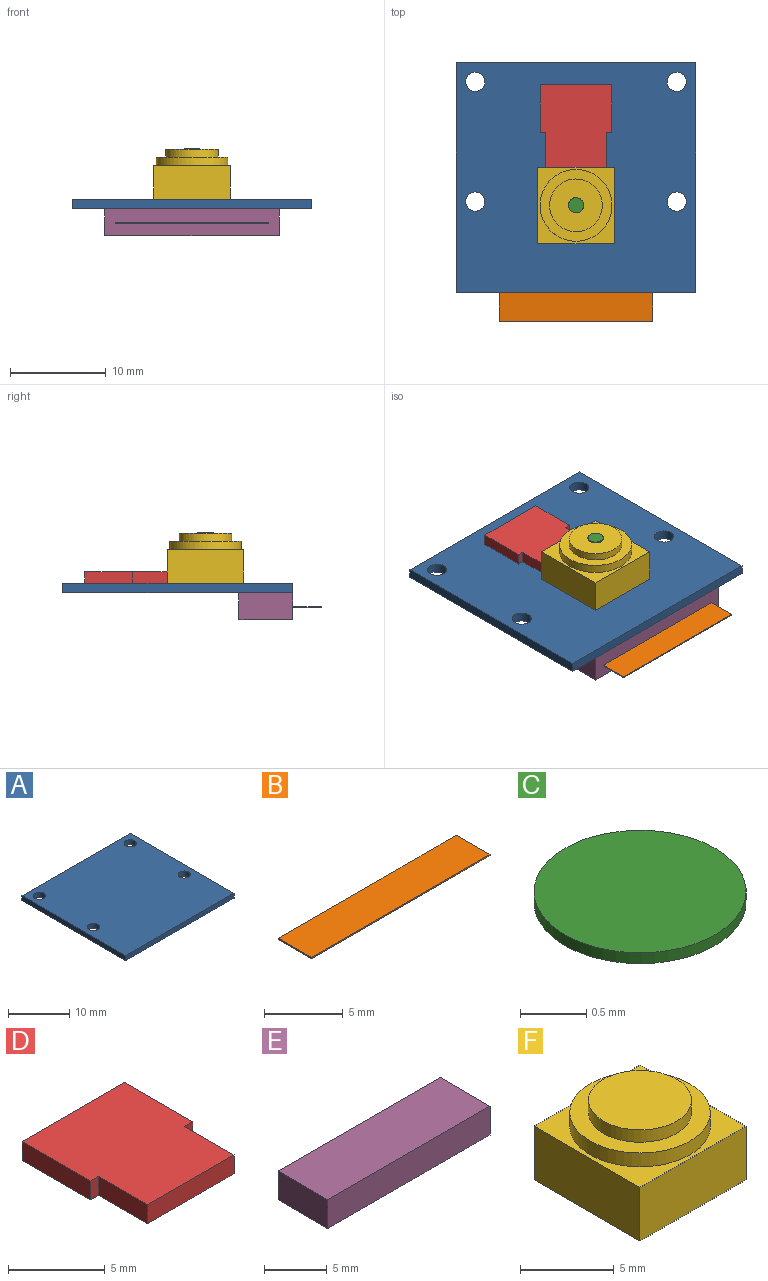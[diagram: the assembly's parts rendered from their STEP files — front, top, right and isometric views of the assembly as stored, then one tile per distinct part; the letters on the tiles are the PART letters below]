
ASSEMBLY  parts=6 mates=5
PART A: 10 faces, bbox 25x24x1 mm
  f0: plane 24x1mm, normal (1,0,0), area 24mm2, adj f1,f7,f8,f9
  f1: plane 25x1mm, normal (0,1,0), area 25mm2, adj f0,f2,f8,f9
  f2: plane 24x1mm, normal (-1,0,0), area 24mm2, adj f1,f7,f8,f9
  f3: cylinder r=1mm len=2mm, axis (0,0,-1), area 6.3mm2, adj f8,f9
  f4: cylinder r=1mm len=2mm, axis (0,0,-1), area 6.3mm2, adj f8,f9
  f5: cylinder r=1mm len=2mm, axis (0,0,-1), area 6.3mm2, adj f8,f9
  f6: cylinder r=1mm len=2mm, axis (0,0,-1), area 6.3mm2, adj f8,f9
  f7: plane 25x1mm, normal (0,-1,0), area 25mm2, adj f0,f2,f8,f9
  f8: plane 25x24mm, normal (0,0,1), area 587.4mm2, adj f0,f1,f2,f3,f4,f5,f6,f7
  f9: plane 25x24mm, normal (0,0,-1), area 587.4mm2, adj f0,f1,f2,f3,f4,f5,f6,f7
PART B: 6 faces, bbox 16x3x0.1 mm
  f0: plane 16x0.1mm, normal (0,-1,0), area 1.6mm2, adj f1,f3,f4,f5
  f1: plane 3x0.1mm, normal (-1,0,0), area 0.3mm2, adj f0,f2,f4,f5
  f2: plane 16x0.1mm, normal (0,1,0), area 1.6mm2, adj f1,f3,f4,f5
  f3: plane 3x0.1mm, normal (1,0,0), area 0.3mm2, adj f0,f2,f4,f5
  f4: plane 16x3mm, normal (0,0,-1), area 48mm2, adj f0,f1,f2,f3
  f5: plane 16x3mm, normal (0,0,1), area 48mm2, adj f0,f1,f2,f3
PART C: 3 faces, bbox 1.6x1.6x0.1 mm
  f0: cylinder r=0.8mm len=1.6mm, axis (0,0,-1), area 0.5mm2, adj f1,f2
  f1: plane 1.6x1.6mm, normal (0,0,1), area 2mm2, adj f0
  f2: plane 1.6x1.6mm, normal (0,0,-1), area 2mm2, adj f0
PART D: 10 faces, bbox 7.5x8.6x1.2 mm
  f0: plane 7.5x1.2mm, normal (0,1,0), area 9mm2, adj f1,f7,f8,f9
  f1: plane 5x1.2mm, normal (-1,0,0), area 6mm2, adj f0,f2,f8,f9
  f2: plane 1.2x0.6mm, normal (0,-1,0), area 0.7mm2, adj f1,f3,f8,f9
  f3: plane 3.6x1.2mm, normal (-1,0,0), area 4.3mm2, adj f2,f4,f8,f9
  f4: plane 6.3x1.2mm, normal (0,-1,0), area 7.6mm2, adj f3,f5,f8,f9
  f5: plane 3.6x1.2mm, normal (1,0,0), area 4.3mm2, adj f4,f6,f8,f9
  f6: plane 1.2x0.6mm, normal (0,-1,0), area 0.7mm2, adj f5,f7,f8,f9
  f7: plane 5x1.2mm, normal (1,0,0), area 6mm2, adj f0,f6,f8,f9
  f8: plane 8.6x7.5mm, normal (0,0,1), area 60.2mm2, adj f0,f1,f2,f3,f4,f5,f6,f7
  f9: plane 8.6x7.5mm, normal (0,0,-1), area 60.2mm2, adj f0,f1,f2,f3,f4,f5,f6,f7
PART E: 6 faces, bbox 18.2x5.6x2.8 mm
  f0: plane 5.6x2.8mm, normal (-1,0,0), area 15.7mm2, adj f1,f3,f4,f5
  f1: plane 18.2x2.8mm, normal (0,1,0), area 51mm2, adj f0,f2,f4,f5
  f2: plane 5.6x2.8mm, normal (1,0,0), area 15.7mm2, adj f1,f3,f4,f5
  f3: plane 18.2x2.8mm, normal (0,-1,0), area 51mm2, adj f0,f2,f4,f5
  f4: plane 18.2x5.6mm, normal (0,0,-1), area 101.9mm2, adj f0,f1,f2,f3
  f5: plane 18.2x5.6mm, normal (0,0,1), area 101.9mm2, adj f0,f1,f2,f3
PART F: 10 faces, bbox 8x8x5.2 mm
  f0: plane 8x3.5mm, normal (1,0,0), area 28mm2, adj f1,f3,f4,f5
  f1: plane 8x3.5mm, normal (0,1,0), area 28mm2, adj f0,f2,f4,f5
  f2: plane 8x3.5mm, normal (-1,0,0), area 28mm2, adj f1,f3,f4,f5
  f3: plane 8x3.5mm, normal (0,-1,0), area 28mm2, adj f0,f2,f4,f5
  f4: plane 8x8mm, normal (0,0,1), area 19.8mm2, adj f0,f1,f2,f3,f6
  f5: plane 8x8mm, normal (0,0,-1), area 64mm2, adj f0,f1,f2,f3
  f6: cylinder r=3.75mm len=7.5mm, axis (0,0,-1), area 21.2mm2, adj f4,f7
  f7: plane 7.5x7.5mm, normal (0,0,1), area 20.4mm2, adj f6,f8
  f8: cylinder r=2.75mm len=5.5mm, axis (0,0,-1), area 13.8mm2, adj f7,f9
  f9: plane 5.5x5.5mm, normal (0,0,1), area 23.8mm2, adj f8
PLACE A t=(-0.11,-0.28,6.89)mm
PLACE B t=(-0.11,-0.28,6.84)mm
PLACE C t=(-0.11,-0.28,6.89)mm
PLACE D t=(-0.11,-0.28,6.89)mm
PLACE E t=(-0.11,-0.28,6.89)mm
PLACE F t=(-0.11,-0.28,6.89)mm
MATE fastened E.f3 <-> B.f2  axis (0,-1,0) through (-0.11,-12.28,4.09)mm
MATE fastened F.f5 <-> A.f8  axis (0,0,-1) through (-0.11,-7.18,7.89)mm
MATE fastened C.f0 <-> F.f6  axis (0,0,-1) through (-0.11,-3.18,13.09)mm
MATE fastened E.f5 <-> A.f9  axis (0,0,1) through (-0.11,-12.28,6.89)mm
MATE fastened A.f8 <-> D.f9  axis (0,0,1) through (-0.11,11.72,7.89)mm
